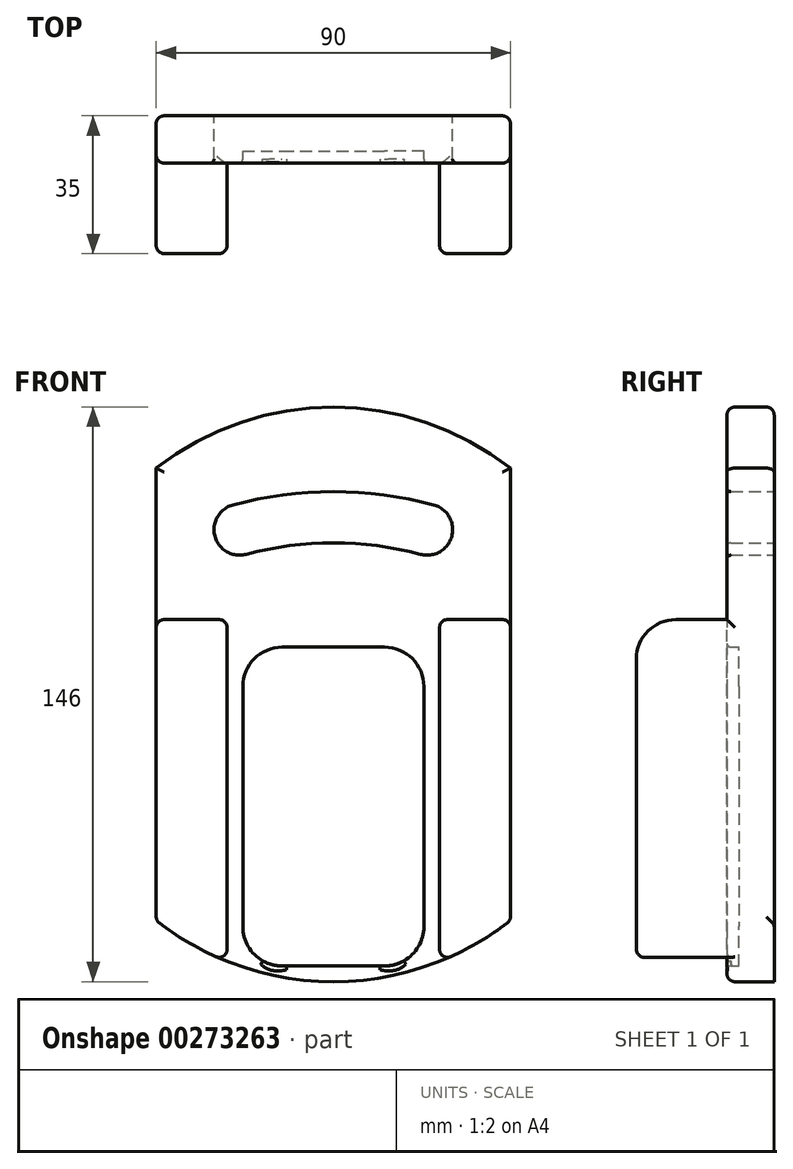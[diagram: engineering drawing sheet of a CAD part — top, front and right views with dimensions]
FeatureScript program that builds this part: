
annotation { "Feature Type Name" : "Feature", "Feature Type Description" : "" }
export const myFeature = defineFeature(function(context is Context, id is Id, definition is map)
    precondition{}
    {
        {
            var Q0;
            Q0=qCreatedBy(makeId("Front.planeOp"),FACE);
            var sketch = newSketch(context, id + "F0", { "sketchPlane" : qUnion([Q0])});
            skArc(sketch, "E0", {"start": v(-64.1, 66) * mm, "mid": v(-68.37, 61.56) * mm, "end": v(-72.33, 56.85) * mm, "construction": true});
            skLineSegment(sketch, "E1", {"start": v(-143.37, -26) * mm, "end": v(175.64, -26) * mm, "construction": true});
            skLineSegment(sketch, "E2", {"start": v(175.64, 112) * mm, "end": v(-105.2, 112) * mm, "construction": true});
            skLineSegment(sketch, "E3", {"start": v(0, -126.13) * mm, "end": v(0, 143.49) * mm, "construction": true});
            skLineSegment(sketch, "E4", {"start": v(38.78, 144.71) * mm, "end": v(0, 0) * mm, "construction": true});
            skLineSegment(sketch, "E5", {"start": v(0, 0) * mm, "end": v(-38.45, 143.49) * mm, "construction": true});
            skLineSegment(sketch, "E6", {"start": v(-70.48, 66) * mm, "end": v(-64.1, 66) * mm, "construction": true});
            skLineSegment(sketch, "E7.top", {"start": v(-27, 66) * mm, "end": v(27, 66) * mm});
            skLineSegment(sketch, "E7.left", {"start": v(-27, -20.82) * mm, "end": v(-27, 66) * mm});
            skLineSegment(sketch, "E7.right", {"start": v(27, -20.82) * mm, "end": v(27, 66) * mm});
            skPoint(sketch, "E8.orphan", {"position": v(-27, -26) * mm});
            skPoint(sketch, "E7.bottom.end.orphan", {"position": v(27, -26) * mm});
            skArc(sketch, "E9", {"start": v(-27, -20.82) * mm, "mid": v(0, -26) * mm, "end": v(27, -20.82) * mm});
            skArc(sketch, "E10", {"start": v(27, -20.82) * mm, "mid": v(36.37, -16.3) * mm, "end": v(45, -10.48) * mm});
            skLineSegment(sketch, "E11.bottom", {"start": v(-27, -26) * mm, "end": v(27, -26) * mm});
            skLineSegment(sketch, "E11.top", {"start": v(-45, 66) * mm, "end": v(45, 66) * mm});
            skLineSegment(sketch, "E12", {"start": v(-45, -10.48) * mm, "end": v(-45, 66) * mm});
            skLineSegment(sketch, "E13", {"start": v(45, -10.48) * mm, "end": v(45, 66) * mm});
            skArc(sketch, "E14", {"start": v(-45, -10.48) * mm, "mid": v(-36.37, -16.3) * mm, "end": v(-27, -20.82) * mm});
            skArc(sketch, "E15", {"start": v(45, 104.48) * mm, "mid": v(0, 120) * mm, "end": v(-45, 104.48) * mm});
            skPoint(sketch, "E16.orphan", {"position": v(-45, -26) * mm});
            skPoint(sketch, "E11.right.start.orphan", {"position": v(45, -26) * mm});
            skLineSegment(sketch, "E17.bottom", {"start": v(-13, 59) * mm, "end": v(13, 59) * mm});
            skLineSegment(sketch, "E17.top", {"start": v(-13, -22) * mm, "end": v(13, -22) * mm});
            skLineSegment(sketch, "E17.left", {"start": v(-23, 49) * mm, "end": v(-23, -12) * mm});
            skLineSegment(sketch, "E17.right", {"start": v(23, 49) * mm, "end": v(23, -12) * mm});
            skPoint(sketch, "E18.visualSharp", {"position": v(-23, 59) * mm});
            skArc(sketch, "E18.filletArc", {"start": v(-13, 59) * mm, "mid": v(-20.07, 56.07) * mm, "end": v(-23, 49) * mm});
            skPoint(sketch, "E19.visualSharp", {"position": v(23, 59) * mm});
            skArc(sketch, "E19.filletArc", {"start": v(23, 49) * mm, "mid": v(20.07, 56.07) * mm, "end": v(13, 59) * mm});
            skPoint(sketch, "E20.visualSharp", {"position": v(23, -22) * mm});
            skArc(sketch, "E20.filletArc", {"start": v(13, -22) * mm, "mid": v(20.07, -19.07) * mm, "end": v(23, -12) * mm});
            skPoint(sketch, "E21.visualSharp", {"position": v(-23, -22) * mm});
            skArc(sketch, "E21.filletArc", {"start": v(-23, -12) * mm, "mid": v(-20.07, -19.07) * mm, "end": v(-13, -22) * mm});
            skArc(sketch, "E22", {"start": v(-25.5, 95.14) * mm, "mid": v(-30.09, 87.18) * mm, "end": v(-22.13, 82.59) * mm});
            skArc(sketch, "E23", {"start": v(22.13, 82.59) * mm, "mid": v(30.09, 87.18) * mm, "end": v(25.5, 95.14) * mm});
            skArc(sketch, "E24.trimOffspring", {"start": v(25.5, 95.14) * mm, "mid": v(0, 98.5) * mm, "end": v(-25.5, 95.14) * mm});
            skArc(sketch, "E25.trimOffspring", {"start": v(22.13, 82.59) * mm, "mid": v(0, 85.5) * mm, "end": v(-22.13, 82.59) * mm});
            skLineSegment(sketch, "E26", {"start": v(-45, -10.48) * mm, "end": v(-45, 104.48) * mm});
            skLineSegment(sketch, "E27", {"start": v(45, -10.48) * mm, "end": v(45, 170.85) * mm});
            skArc(sketch, "E28.trimOffspring", {"start": v(-70.48, 66) * mm, "mid": v(-71.55, 61.46) * mm, "end": v(-72.33, 56.85) * mm, "construction": true});
            skLineSegment(sketch, "E29.trimOffspring", {"start": v(-45, 66) * mm, "end": v(236.1, 66) * mm, "construction": true});
            skArc(sketch, "E30.trimOffspring", {"start": v(23.81, 88.87) * mm, "mid": v(0, 92) * mm, "end": v(-23.81, 88.87) * mm, "construction": true});
            skSolve(sketch);
        }
        {
            var Q0;
            {var subQ0=sQuery(id+"F0.wireOp",EDGE,"E7.left");Q0=makeQuery(id+"F0.imprint","IMPRINT",FACE,{"disambiguationData":[TD([[makeQuery(id+"F0.imprint","IMPRINT",EDGE,{"derivedFrom":subQ0}),1.0]])]});}
            var Q1;
            {var subQ0=sQuery(id+"F0.wireOp",EDGE,"E7.right");Q1=makeQuery(id+"F0.imprint","IMPRINT",FACE,{"disambiguationData":[TD([[makeQuery(id+"F0.imprint","IMPRINT",EDGE,{"derivedFrom":subQ0}),-1.0]])]});}
            extrude(context, id + "F1", {"entities" : qUnion([Q0, Q1]), "depth" : 35 * mm});
        }
        {
            var Q0;
            {var subQ0=sQuery(id+"F0.wireOp",EDGE,"E7.left");Q0=makeQuery(id+"F0.imprint","IMPRINT",FACE,{"disambiguationData":[TD([[makeQuery(id+"F0.imprint","IMPRINT",EDGE,{"derivedFrom":subQ0}),-1.0]])]});}
            var Q1;
            {var subQ0=sQuery(id+"F0.wireOp",EDGE,"E15");Q1=makeQuery(id+"F0.imprint","IMPRINT",FACE,{"disambiguationData":[TD([[makeQuery(id+"F0.imprint","IMPRINT",EDGE,{"derivedFrom":subQ0}),1.0]])]});}
            extrude(context, id + "F2", {"entities" : qUnion([Q0, Q1]), "operationType" : NewBodyOperationType.ADD, "depth" : 12 * mm});
        }
        {
            var Q0;
            Q0=makeQuery(id+"F0.imprint","IMPRINT",FACE,{"disambiguationData":[TD([[makeQuery(id+"F0.imprint","IMPRINT",EDGE,{"derivedFrom":sQuery(id+"F0.wireOp",EDGE,"E17.bottom")}),-1.0]])]});
            extrude(context, id + "F3", {"entities" : qUnion([Q0]), "operationType" : NewBodyOperationType.ADD, "depth" : 9 * mm});
        }
        {
            var Q0;
            Q0=makeQuery(id+"F2.opExtrude","CAP_EDGE",EDGE,{"disambiguationData":[OSD([sQuery(id+"F0.wireOp",EDGE,"E25.trimOffspring")])],"isStart":false});
            var Q1;
            Q1=makeQuery(id+"F2.opExtrude","CAP_EDGE",EDGE,{"disambiguationData":[OSD([sQuery(id+"F0.wireOp",EDGE,"E22")])],"isStart":false});
            var Q2;
            Q2=makeQuery(id+"F2.opExtrude","CAP_EDGE",EDGE,{"disambiguationData":[OSD([sQuery(id+"F0.wireOp",EDGE,"E23")])],"isStart":false});
            var Q3;
            Q3=makeQuery(id+"F2.opExtrude","CAP_EDGE",EDGE,{"disambiguationData":[OSD([sQuery(id+"F0.wireOp",EDGE,"E24.trimOffspring")])],"isStart":false});
            fillet(context, id + "F4", {"entities" : qUnion([Q0, Q1, Q2, Q3]), "radius" : 1 * mm, "tangentPropagation" : true, "allowEdgeOverflow" : false});
        }
        {
            var Q0;
            {var subQ0=sQuery(id+"F0.wireOp",EDGE,"E27");Q0=makeQuery(id+"F2.boolean.opBoolean","MERGE",FACE,{"derivedFrom":[makeQuery(id+"F1.opExtrude","SWEPT_FACE",FACE,{"disambiguationData":[OSD([subQ0])]}),makeQuery(id+"F2.opExtrude","SWEPT_FACE",FACE,{"disambiguationData":[OSD([subQ0])]})]});}
            var sketch = newSketch(context, id + "F5", { "sketchPlane" : qUnion([Q0])});
            skLineSegment(sketch, "E31.0", {"start": v(-25, 66) * mm, "end": v(-12, 66) * mm});
            skLineSegment(sketch, "E31.1", {"start": v(-35, -10.48) * mm, "end": v(-35, 56) * mm});
            skPoint(sketch, "E32.visualSharp", {"position": v(-35, 66) * mm});
            skArc(sketch, "E32.filletArc", {"start": v(-25, 66) * mm, "mid": v(-32.07, 63.07) * mm, "end": v(-35, 56) * mm});
            skSolve(sketch);
        }
        {
            var Q0;
            {var subQ0=sQuery(id+"F5.wireOp",EDGE,"E32.filletArc");Q0=makeQuery(id+"F5.imprint","IMPRINT",FACE,{"disambiguationData":[TD([[makeQuery(id+"F5.imprint","IMPRINT",EDGE,{"derivedFrom":subQ0}),-1.0]])]});}
            extrude(context, id + "F6", {"entities" : qUnion([Q0]), "operationType" : NewBodyOperationType.REMOVE, "endBound" : BoundingType.THROUGH_ALL, "oppositeDirection" : true, "depth" : 25 * mm});
        }
        {
            var Q0;
            Q0=makeQuery(id+"F2.opExtrude","CAP_EDGE",EDGE,{"disambiguationData":[OSD([sQuery(id+"F0.wireOp",EDGE,"E27")])],"isStart":false});
            var Q1;
            Q1=makeQuery(id+"F2.opExtrude","CAP_EDGE",EDGE,{"disambiguationData":[OSD([sQuery(id+"F0.wireOp",EDGE,"E15")])],"isStart":false});
            var Q2;
            Q2=makeQuery(id+"F2.opExtrude","CAP_EDGE",EDGE,{"disambiguationData":[OSD([sQuery(id+"F0.wireOp",EDGE,"E26")])],"isStart":false});
            var Q3;
            Q3=makeQuery(id+"F6.boolean.opBoolean","COPY",EDGE,{"derivedFrom":makeQuery(id+"F6.opExtrude","CAP_EDGE",EDGE,{"disambiguationData":[OSD([sQuery(id+"F5.wireOp",EDGE,"E32.filletArc")])],"isStart":true})});
            var Q4;
            Q4=makeQuery(id+"F1.opExtrude","SWEPT_EDGE",EDGE,{"disambiguationData":[OSD([sQuery(id+"F0.wireOp",EDGE,"E11.top"),sQuery(id+"F0.wireOp",EDGE,"E27")])]});
            var Q5;
            Q5=makeQuery(id+"F1.opExtrude","CAP_EDGE",EDGE,{"disambiguationData":[OSD([sQuery(id+"F0.wireOp",EDGE,"E27")])],"isStart":false});
            var Q6;
            Q6=makeQuery(id+"F1.opExtrude","SWEPT_EDGE",EDGE,{"disambiguationData":[OSD([sQuery(id+"F0.wireOp",EDGE,"E10"),sQuery(id+"F0.wireOp",EDGE,"E27")])]});
            var Q7;
            {var subQ0=sQuery(id+"F0.wireOp",EDGE,"E27");Q7=makeQuery(id+"F2.boolean.opBoolean","MERGE",EDGE,{"derivedFrom":[makeQuery(id+"F1.opExtrude","CAP_EDGE",EDGE,{"disambiguationData":[OSD([subQ0])],"isStart":true}),makeQuery(id+"F2.opExtrude","CAP_EDGE",EDGE,{"disambiguationData":[OSD([subQ0])],"isStart":true})]});}
            var Q8;
            Q8=makeQuery(id+"F2.opExtrude","CAP_EDGE",EDGE,{"disambiguationData":[OSD([sQuery(id+"F0.wireOp",EDGE,"E15")])],"isStart":true});
            var Q9;
            {var subQ0=sQuery(id+"F0.wireOp",EDGE,"E26");Q9=makeQuery(id+"F2.boolean.opBoolean","MERGE",EDGE,{"derivedFrom":[makeQuery(id+"F1.opExtrude","CAP_EDGE",EDGE,{"disambiguationData":[OSD([subQ0])],"isStart":true}),makeQuery(id+"F2.opExtrude","CAP_EDGE",EDGE,{"disambiguationData":[OSD([subQ0])],"isStart":true})]});}
            var Q10;
            Q10=makeQuery(id+"F1.opExtrude","SWEPT_EDGE",EDGE,{"disambiguationData":[OSD([sQuery(id+"F0.wireOp",EDGE,"E14"),sQuery(id+"F0.wireOp",EDGE,"E26")])]});
            var Q11;
            Q11=makeQuery(id+"F1.opExtrude","CAP_EDGE",EDGE,{"disambiguationData":[OSD([sQuery(id+"F0.wireOp",EDGE,"E26")])],"isStart":false});
            var Q12;
            {var subQ0=sQuery(id+"F0.wireOp",EDGE,"E26");Q12=makeQuery(id+"F6.boolean.opBoolean","INTERSECT",EDGE,{"derivedFrom":[makeQuery(id+"F2.boolean.opBoolean","MERGE",FACE,{"derivedFrom":[makeQuery(id+"F1.opExtrude","SWEPT_FACE",FACE,{"disambiguationData":[OSD([subQ0])]}),makeQuery(id+"F2.opExtrude","SWEPT_FACE",FACE,{"disambiguationData":[OSD([subQ0])]})]}),makeQuery(id+"F6.opExtrude","SWEPT_FACE",FACE,{"disambiguationData":[OSD([sQuery(id+"F5.wireOp",EDGE,"E32.filletArc")])]})]});}
            var Q13;
            Q13=makeQuery(id+"F1.opExtrude","SWEPT_EDGE",EDGE,{"disambiguationData":[OSD([sQuery(id+"F0.wireOp",EDGE,"E11.top"),sQuery(id+"F0.wireOp",EDGE,"E26")])]});
            var Q14;
            Q14=makeQuery(id+"F1.opExtrude","CAP_EDGE",EDGE,{"disambiguationData":[OSD([sQuery(id+"F0.wireOp",EDGE,"E14")])],"isStart":false});
            var Q15;
            Q15=makeQuery(id+"F1.opExtrude","SWEPT_EDGE",EDGE,{"disambiguationData":[OSD([sQuery(id+"F0.wireOp",EDGE,"E7.left"),sQuery(id+"F0.wireOp",EDGE,"E9"),sQuery(id+"F0.wireOp",EDGE,"E14")])]});
            var Q16;
            Q16=makeQuery(id+"F2.opExtrude","CAP_EDGE",EDGE,{"disambiguationData":[OSD([sQuery(id+"F0.wireOp",EDGE,"E9")])],"isStart":false});
            var Q17;
            Q17=makeQuery(id+"F1.opExtrude","SWEPT_EDGE",EDGE,{"disambiguationData":[OSD([sQuery(id+"F0.wireOp",EDGE,"E7.right"),sQuery(id+"F0.wireOp",EDGE,"E9"),sQuery(id+"F0.wireOp",EDGE,"E10")])]});
            var Q18;
            Q18=makeQuery(id+"F1.opExtrude","CAP_EDGE",EDGE,{"disambiguationData":[OSD([sQuery(id+"F0.wireOp",EDGE,"E10")])],"isStart":false});
            var Q19;
            Q19=makeQuery(id+"F1.opExtrude","CAP_EDGE",EDGE,{"disambiguationData":[OSD([sQuery(id+"F0.wireOp",EDGE,"E7.right")])],"isStart":false});
            var Q20;
            Q20=makeQuery(id+"F6.boolean.opBoolean","INTERSECT",EDGE,{"derivedFrom":[makeQuery(id+"F1.opExtrude","SWEPT_FACE",FACE,{"disambiguationData":[OSD([sQuery(id+"F0.wireOp",EDGE,"E7.right")])]}),makeQuery(id+"F6.opExtrude","SWEPT_FACE",FACE,{"disambiguationData":[OSD([sQuery(id+"F5.wireOp",EDGE,"E32.filletArc")])]})]});
            var Q21;
            Q21=makeQuery(id+"F1.opExtrude","SWEPT_EDGE",EDGE,{"disambiguationData":[OSD([sQuery(id+"F0.wireOp",EDGE,"E7.right"),sQuery(id+"F0.wireOp",EDGE,"E11.top")])]});
            var Q22;
            Q22=makeQuery(id+"F1.opExtrude","SWEPT_EDGE",EDGE,{"disambiguationData":[OSD([sQuery(id+"F0.wireOp",EDGE,"E7.left"),sQuery(id+"F0.wireOp",EDGE,"E11.top")])]});
            var Q23;
            Q23=makeQuery(id+"F6.boolean.opBoolean","INTERSECT",EDGE,{"derivedFrom":[makeQuery(id+"F1.opExtrude","SWEPT_FACE",FACE,{"disambiguationData":[OSD([sQuery(id+"F0.wireOp",EDGE,"E7.left")])]}),makeQuery(id+"F6.opExtrude","SWEPT_FACE",FACE,{"disambiguationData":[OSD([sQuery(id+"F5.wireOp",EDGE,"E32.filletArc")])]})]});
            var Q24;
            Q24=makeQuery(id+"F1.opExtrude","CAP_EDGE",EDGE,{"disambiguationData":[OSD([sQuery(id+"F0.wireOp",EDGE,"E7.left")])],"isStart":false});
            fillet(context, id + "F7", {"entities" : qUnion([Q0, Q1, Q2, Q3, Q4, Q5, Q6, Q7, Q8, Q9, Q10, Q11, Q12, Q13, Q14, Q15, Q16, Q17, Q18, Q19, Q20, Q21, Q22, Q23, Q24]), "radius" : 2 * mm, "tangentPropagation" : true, "allowEdgeOverflow" : false});
        }
        {
            var Q0;
            Q0=makeQuery(id+"F2.opExtrude","CAP_EDGE",EDGE,{"disambiguationData":[OSD([sQuery(id+"F0.wireOp",EDGE,"E17.right")])],"isStart":false});
            var Q1;
            Q1=makeQuery(id+"F2.opExtrude","CAP_EDGE",EDGE,{"disambiguationData":[OSD([sQuery(id+"F0.wireOp",EDGE,"E18.filletArc")])],"isStart":false});
            var Q2;
            Q2=makeQuery(id+"F2.opExtrude","CAP_EDGE",EDGE,{"disambiguationData":[OSD([sQuery(id+"F0.wireOp",EDGE,"E17.left")])],"isStart":false});
            var Q3;
            Q3=makeQuery(id+"F2.opExtrude","CAP_EDGE",EDGE,{"disambiguationData":[OSD([sQuery(id+"F0.wireOp",EDGE,"E21.filletArc")])],"isStart":false});
            var Q4;
            Q4=makeQuery(id+"F2.opExtrude","CAP_EDGE",EDGE,{"disambiguationData":[OSD([sQuery(id+"F0.wireOp",EDGE,"E17.top")])],"isStart":false});
            var Q5;
            Q5=makeQuery(id+"F2.opExtrude","CAP_EDGE",EDGE,{"disambiguationData":[OSD([sQuery(id+"F0.wireOp",EDGE,"E20.filletArc")])],"isStart":false});
            var Q6;
            Q6=makeQuery(id+"F2.opExtrude","CAP_EDGE",EDGE,{"disambiguationData":[OSD([sQuery(id+"F0.wireOp",EDGE,"E19.filletArc")])],"isStart":false});
            var Q7;
            Q7=makeQuery(id+"F2.opExtrude","CAP_EDGE",EDGE,{"disambiguationData":[OSD([sQuery(id+"F0.wireOp",EDGE,"E17.bottom")])],"isStart":false});
            fillet(context, id + "F8", {"entities" : qUnion([Q0, Q1, Q2, Q3, Q4, Q5, Q6, Q7]), "radius" : 1 * mm, "tangentPropagation" : true, "allowEdgeOverflow" : false});
        }
    });
